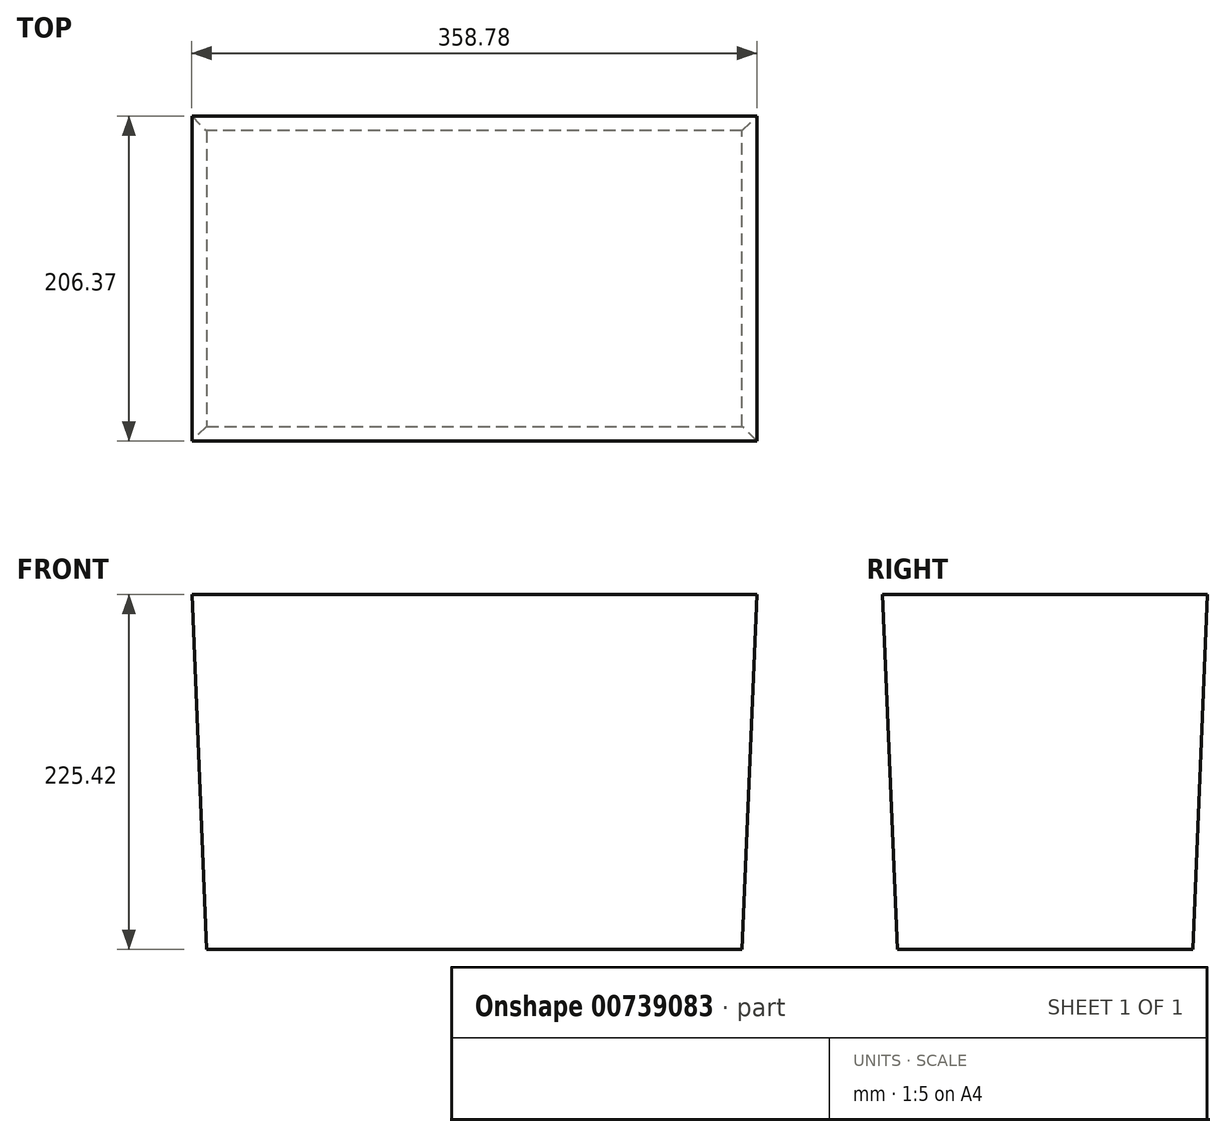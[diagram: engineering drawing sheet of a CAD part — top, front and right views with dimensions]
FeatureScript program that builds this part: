
annotation { "Feature Type Name" : "Feature", "Feature Type Description" : "" }
export const myFeature = defineFeature(function(context is Context, id is Id, definition is map)
    precondition{}
    {
        {
            var Q0;
            Q0=qCreatedBy(makeId("Top.planeOp"),FACE);
            var sketch = newSketch(context, id + "F0", { "sketchPlane" : qUnion([Q0])});
            skLineSegment(sketch, "E0.bottom", {"start": v(-179.39, 98.54) * mm, "end": v(179.39, 98.54) * mm});
            skLineSegment(sketch, "E0.top", {"start": v(-179.39, -107.83) * mm, "end": v(179.39, -107.83) * mm});
            skLineSegment(sketch, "E0.left", {"start": v(-179.39, 98.54) * mm, "end": v(-179.39, -107.83) * mm});
            skLineSegment(sketch, "E0.right", {"start": v(179.39, 98.54) * mm, "end": v(179.39, -107.83) * mm});
            skPoint(sketch, "E0.middle", {"position": v(0, -4.65) * mm});
            skSolve(sketch);
        }
        {
            var Q0;
            Q0 = qSketchRegion(id + "F0", true);
            extrude(context, id + "F1", {"entities" : qUnion([Q0]), "oppositeDirection" : true, "depth" : 225.42 * mm, "offsetDistance" : 25.4 * mm, "hasDraft" : true, "draftAngle" : 2.38 * degree, "draftPullDirection" : true});
        }
    });
